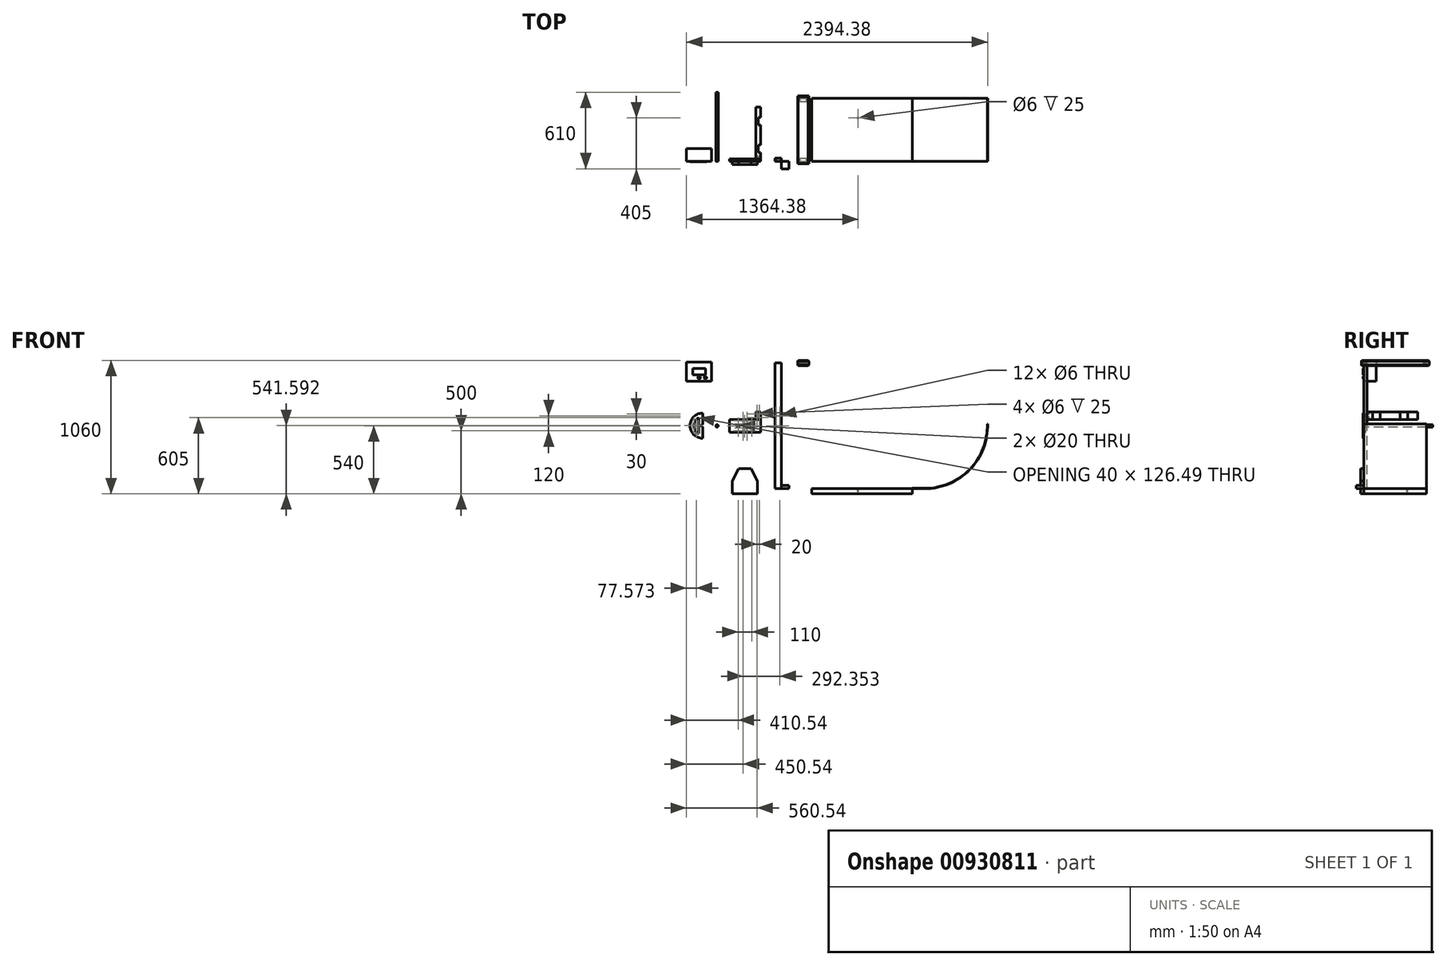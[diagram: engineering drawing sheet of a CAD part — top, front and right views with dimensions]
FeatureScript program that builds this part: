
annotation { "Feature Type Name" : "Feature", "Feature Type Description" : "" }
export const myFeature = defineFeature(function(context is Context, id is Id, definition is map)
    precondition{}
    {
        {
            var Q0;
            Q0=qCreatedBy(makeId("Top.planeOp"),FACE);
            var sketch = newSketch(context, id + "F0", { "sketchPlane" : qUnion([Q0])});
            skLineSegment(sketch, "E0.bottom", {"start": v(-400, 250) * mm, "end": v(400, 250) * mm});
            skLineSegment(sketch, "E0.top", {"start": v(-400, -250) * mm, "end": v(400, -250) * mm});
            skLineSegment(sketch, "E0.left", {"start": v(-400, 250) * mm, "end": v(-400, -250) * mm});
            skLineSegment(sketch, "E0.right", {"start": v(400, 250) * mm, "end": v(400, -250) * mm});
            skPoint(sketch, "E0.middle", {"position": v(0, 0) * mm});
            skSolve(sketch);
        }
        {
            var Q0;
            Q0 = qSketchRegion(id + "F0", true);
            extrude(context, id + "F1", {"entities" : qUnion([Q0]), "depth" : 40 * mm, "offsetDistance" : 25 * mm});
        }
        {
            var Q0;
            Q0=makeQuery(id+"F1.opExtrude","SWEPT_FACE",FACE,{"disambiguationData":[OSD([sQuery(id+"F0.wireOp",EDGE,"E0.top")])]});
            var sketch = newSketch(context, id + "F2", { "sketchPlane" : qUnion([Q0])});
            skLineSegment(sketch, "E1.bottom", {"start": v(-641.49, 40) * mm, "end": v(-691.49, 40) * mm});
            skLineSegment(sketch, "E1.top", {"start": v(-641.49, 1040) * mm, "end": v(-691.49, 1040) * mm});
            skLineSegment(sketch, "E1.left", {"start": v(-641.49, 40) * mm, "end": v(-641.49, 1040) * mm});
            skLineSegment(sketch, "E1.right", {"start": v(-691.49, 40) * mm, "end": v(-691.49, 1040) * mm});
            skCircle(sketch, "E2", {"center": v(-651.49, 620) * mm, "radius": 3 * mm});
            skCircle(sketch, "E3", {"center": v(-681.49, 620) * mm, "radius": 3 * mm});
            skCircle(sketch, "E4.MirrorC", {"center": v(-651.49, 540) * mm, "radius": 3 * mm});
            skCircle(sketch, "E5.MirrorC", {"center": v(-681.49, 540) * mm, "radius": 3 * mm});
            skSolve(sketch);
        }
        {
            var Q0;
            Q0=makeQuery(id+"F2.imprint","IMPRINT",FACE,{"disambiguationData":[TD([[makeQuery(id+"F2.imprint","IMPRINT",EDGE,{"derivedFrom":sQuery(id+"F2.wireOp",EDGE,"E1.bottom")}),-1.0]])]});
            extrude(context, id + "F3", {"entities" : qUnion([Q0]), "oppositeDirection" : true, "depth" : 25 * mm, "offsetDistance" : 25 * mm});
        }
        {
            var Q0;
            Q0=makeQuery(id+"F1.opExtrude","SWEPT_FACE",FACE,{"disambiguationData":[OSD([sQuery(id+"F0.wireOp",EDGE,"E0.top")])]});
            var sketch = newSketch(context, id + "F4", { "sketchPlane" : qUnion([Q0])});
            skLineSegment(sketch, "E6.bottom", {"start": v(-829.9, 0) * mm, "end": v(-1029.9, 0) * mm});
            skLineSegment(sketch, "E6.top", {"start": v(-879.9, 200) * mm, "end": v(-979.9, 200) * mm});
            skLineSegment(sketch, "E6.left", {"start": v(-829.9, 0) * mm, "end": v(-829.9, 100) * mm});
            skLineSegment(sketch, "E6.right", {"start": v(-1029.9, 0) * mm, "end": v(-1029.9, 100) * mm});
            skLineSegment(sketch, "E7", {"start": v(-1029.9, 100) * mm, "end": v(-979.9, 200) * mm});
            skLineSegment(sketch, "E8", {"start": v(-829.9, 100) * mm, "end": v(-879.9, 200) * mm});
            skSolve(sketch);
        }
        {
            var Q0;
            Q0 = qSketchRegion(id + "F4", true);
            extrude(context, id + "F5", {"entities" : qUnion([Q0]), "depth" : 25 * mm, "offsetDistance" : 25 * mm});
        }
        {
            var Q0;
            Q0=makeQuery(id+"F3.opExtrude","CAP_FACE",FACE,{"disambiguationData":[OSD([sQuery(id+"F2.wireOp",EDGE,"E1.bottom"),sQuery(id+"F2.wireOp",EDGE,"E1.top"),sQuery(id+"F2.wireOp",EDGE,"E1.left"),sQuery(id+"F2.wireOp",EDGE,"E1.right")])],"isStart":true});
            var sketch = newSketch(context, id + "F6", { "sketchPlane" : qUnion([Q0])});
            skLineSegment(sketch, "E9.bottom", {"start": v(-1053.84, 590) * mm, "end": v(-803.84, 590) * mm});
            skLineSegment(sketch, "E9.top", {"start": v(-1053.84, 490) * mm, "end": v(-803.84, 490) * mm});
            skLineSegment(sketch, "E9.left", {"start": v(-1053.84, 590) * mm, "end": v(-1053.84, 490) * mm});
            skLineSegment(sketch, "E9.right", {"start": v(-803.84, 590) * mm, "end": v(-803.84, 490) * mm});
            skPoint(sketch, "E9.middle", {"position": v(-928.84, 540) * mm});
            skPoint(sketch, "E9.middle.positionSnap0", {"position": v(-691.49, 540) * mm});
            skPoint(sketch, "E9.centerSnap0", {"position": v(-691.49, 540) * mm});
            skCircle(sketch, "E10", {"center": v(-873.84, 540) * mm, "radius": 10 * mm});
            skCircle(sketch, "E11", {"center": v(-983.84, 540) * mm, "radius": 10 * mm});
            skCircle(sketch, "E12", {"center": v(-943.84, 580) * mm, "radius": 3 * mm});
            skCircle(sketch, "E13", {"center": v(-913.84, 580) * mm, "radius": 3 * mm});
            skCircle(sketch, "E14.MirrorC", {"center": v(-943.84, 500) * mm, "radius": 3 * mm});
            skCircle(sketch, "E15.MirrorC", {"center": v(-913.84, 500) * mm, "radius": 3 * mm});
            skPoint(sketch, "E16.middle", {"position": v(-933.84, 540) * mm});
            skCircle(sketch, "E17", {"center": v(-913.84, 555) * mm, "radius": 3 * mm});
            skCircle(sketch, "E18", {"center": v(-913.84, 525) * mm, "radius": 3 * mm});
            skCircle(sketch, "E19", {"center": v(-933.84, 525) * mm, "radius": 3 * mm});
            skCircle(sketch, "E20", {"center": v(-933.84, 555) * mm, "radius": 3 * mm});
            skSolve(sketch);
        }
        {
            var Q0;
            Q0=makeQuery(id+"F6.imprint","IMPRINT",FACE,{"disambiguationData":[TD([[makeQuery(id+"F6.imprint","IMPRINT",EDGE,{"derivedFrom":sQuery(id+"F6.wireOp",EDGE,"E9.bottom")}),-1.0]])]});
            extrude(context, id + "F7", {"entities" : qUnion([Q0]), "oppositeDirection" : true, "depth" : 20 * mm, "offsetDistance" : 25 * mm});
        }
        {
            var Q0;
            Q0=makeQuery(id+"F7.opExtrude","CAP_FACE",FACE,{"disambiguationData":[OSD([sQuery(id+"F6.wireOp",EDGE,"E9.bottom"),sQuery(id+"F6.wireOp",EDGE,"E9.top"),sQuery(id+"F6.wireOp",EDGE,"E9.left"),sQuery(id+"F6.wireOp",EDGE,"E9.right"),sQuery(id+"F6.wireOp",EDGE,"E10"),sQuery(id+"F6.wireOp",EDGE,"E11"),sQuery(id+"F6.wireOp",EDGE,"E12"),sQuery(id+"F6.wireOp",EDGE,"E13"),sQuery(id+"F6.wireOp",EDGE,"E14.MirrorC"),sQuery(id+"F6.wireOp",EDGE,"E15.MirrorC")])],"isStart":true});
            var sketch = newSketch(context, id + "F8", { "sketchPlane" : qUnion([Q0])});
            skCircle(sketch, "E21", {"center": v(-1152.55, 540) * mm, "radius": 10 * mm});
            skPoint(sketch, "E21.centerSnap0", {"position": v(-1053.84, 540) * mm});
            skSolve(sketch);
        }
        {
            var Q0;
            Q0 = qSketchRegion(id + "F8", true);
            extrude(context, id + "F9", {"entities" : qUnion([Q0]), "oppositeDirection" : true, "depth" : 550 * mm, "offsetDistance" : 25 * mm});
        }
        {
            var Q0;
            Q0=makeQuery(id+"F7.opExtrude","SWEPT_FACE",FACE,{"disambiguationData":[OSD([sQuery(id+"F6.wireOp",EDGE,"E9.bottom")])]});
            var sketch = newSketch(context, id + "F10", { "sketchPlane" : qUnion([Q0])});
            skLineSegment(sketch, "E22.bottom", {"start": v(-803.84, -230) * mm, "end": v(-843.84, -230) * mm});
            skLineSegment(sketch, "E22.top", {"start": v(-803.84, 180) * mm, "end": v(-843.84, 180) * mm});
            skLineSegment(sketch, "E22.left", {"start": v(-803.84, -230) * mm, "end": v(-803.84, -180) * mm});
            skLineSegment(sketch, "E22.right", {"start": v(-843.84, -230) * mm, "end": v(-843.84, 180) * mm});
            skLineSegment(sketch, "E23", {"start": v(-803.84, -180) * mm, "end": v(-823.84, -180) * mm});
            skLineSegment(sketch, "E24", {"start": v(-823.84, -180) * mm, "end": v(-823.84, -120) * mm});
            skLineSegment(sketch, "E25", {"start": v(-823.84, -120) * mm, "end": v(-803.84, -120) * mm});
            skLineSegment(sketch, "E26.trimOffspring", {"start": v(-803.84, -120) * mm, "end": v(-803.84, 40) * mm});
            skLineSegment(sketch, "E27", {"start": v(-803.84, 100) * mm, "end": v(-823.84, 100) * mm});
            skLineSegment(sketch, "E28", {"start": v(-823.84, 100) * mm, "end": v(-823.84, 40) * mm});
            skLineSegment(sketch, "E29", {"start": v(-823.84, 40) * mm, "end": v(-803.84, 40) * mm});
            skLineSegment(sketch, "E30.trimOffspring", {"start": v(-803.84, 100) * mm, "end": v(-803.84, 180) * mm});
            skSolve(sketch);
        }
        {
            var Q0;
            Q0 = qSketchRegion(id + "F10", true);
            extrude(context, id + "F11", {"entities" : qUnion([Q0]), "operationType" : NewBodyOperationType.ADD, "depth" : 60 * mm, "offsetDistance" : 25 * mm});
        }
        {
            var Q0;
            Q0=makeQuery(id+"F11.opExtrude","SWEPT_FACE",FACE,{"disambiguationData":[OSD([sQuery(id+"F10.wireOp",EDGE,"E22.bottom")])]});
            var sketch = newSketch(context, id + "F12", { "sketchPlane" : qUnion([Q0])});
            skCircle(sketch, "E31", {"center": v(-833.84, 635) * mm, "radius": 3 * mm});
            skCircle(sketch, "E32", {"center": v(-813.84, 635) * mm, "radius": 3 * mm});
            skCircle(sketch, "E33", {"center": v(-833.84, 605) * mm, "radius": 3 * mm});
            skCircle(sketch, "E34", {"center": v(-813.84, 605) * mm, "radius": 3 * mm});
            skSolve(sketch);
        }
        {
            var Q0;
            Q0 = qSketchRegion(id + "F12", true);
            extrude(context, id + "F13", {"entities" : qUnion([Q0]), "operationType" : NewBodyOperationType.REMOVE, "oppositeDirection" : true, "depth" : 25 * mm, "offsetDistance" : 25 * mm});
        }
        {
            var Q0;
            Q0=makeQuery(id+"F3.opExtrude","CAP_FACE",FACE,{"disambiguationData":[OSD([sQuery(id+"F2.wireOp",EDGE,"E1.bottom"),sQuery(id+"F2.wireOp",EDGE,"E1.top"),sQuery(id+"F2.wireOp",EDGE,"E1.left"),sQuery(id+"F2.wireOp",EDGE,"E1.right"),sQuery(id+"F2.wireOp",EDGE,"E2"),sQuery(id+"F2.wireOp",EDGE,"E3"),sQuery(id+"F2.wireOp",EDGE,"E4.MirrorC"),sQuery(id+"F2.wireOp",EDGE,"E5.MirrorC")])],"isStart":true});
            var sketch = newSketch(context, id + "F14", { "sketchPlane" : qUnion([Q0])});
            skLineSegment(sketch, "E35.bottom", {"start": v(-641.49, 40) * mm, "end": v(-581.49, 40) * mm});
            skLineSegment(sketch, "E35.top", {"start": v(-641.49, 65) * mm, "end": v(-581.49, 65) * mm});
            skLineSegment(sketch, "E35.left", {"start": v(-641.49, 40) * mm, "end": v(-641.49, 65) * mm});
            skLineSegment(sketch, "E35.right", {"start": v(-581.49, 40) * mm, "end": v(-581.49, 65) * mm});
            skSolve(sketch);
        }
        {
            var Q0;
            Q0 = qSketchRegion(id + "F14", true);
            extrude(context, id + "F15", {"entities" : qUnion([Q0]), "depth" : 60 * mm, "offsetDistance" : 25 * mm});
        }
        {
            var Q0;
            Q0=makeQuery(id+"F1.opExtrude","CAP_FACE",FACE,{"disambiguationData":[OSD([sQuery(id+"F0.wireOp",EDGE,"E0.bottom"),sQuery(id+"F0.wireOp",EDGE,"E0.top"),sQuery(id+"F0.wireOp",EDGE,"E0.left"),sQuery(id+"F0.wireOp",EDGE,"E0.right")])],"isStart":false});
            var sketch = newSketch(context, id + "F16", { "sketchPlane" : qUnion([Q0])});
            skCircle(sketch, "E36", {"center": v(-30, 95) * mm, "radius": 3 * mm});
            skSolve(sketch);
        }
        {
            var Q0;
            Q0 = qSketchRegion(id + "F16", true);
            extrude(context, id + "F17", {"entities" : qUnion([Q0]), "operationType" : NewBodyOperationType.REMOVE, "oppositeDirection" : true, "depth" : 25 * mm, "offsetDistance" : 25 * mm});
        }
        {
            var Q0;
            Q0=makeQuery(id+"F3.opExtrude","SWEPT_FACE",FACE,{"disambiguationData":[OSD([sQuery(id+"F2.wireOp",EDGE,"E1.top")])]});
            var sketch = newSketch(context, id + "F18", { "sketchPlane" : qUnion([Q0])});
            skLineSegment(sketch, "E37.bottom", {"start": v(-491.35, -250) * mm, "end": v(-441.35, -250) * mm});
            skLineSegment(sketch, "E37.top", {"start": v(-491.35, 250) * mm, "end": v(-441.35, 250) * mm});
            skLineSegment(sketch, "E37.left", {"start": v(-491.35, -250) * mm, "end": v(-491.35, -225) * mm});
            skLineSegment(sketch, "E37.right", {"start": v(-441.35, -250) * mm, "end": v(-441.35, -225) * mm});
            skLineSegment(sketch, "E38.0", {"start": v(-511.35, 270) * mm, "end": v(-421.35, 270) * mm});
            skLineSegment(sketch, "E38.1", {"start": v(-511.35, -270) * mm, "end": v(-511.35, 270) * mm});
            skLineSegment(sketch, "E38.2", {"start": v(-511.35, -270) * mm, "end": v(-421.35, -270) * mm});
            skLineSegment(sketch, "E38.3", {"start": v(-421.35, -270) * mm, "end": v(-421.35, 270) * mm});
            skLineSegment(sketch, "E39", {"start": v(-491.35, -225) * mm, "end": v(-441.35, -225) * mm});
            skLineSegment(sketch, "E40", {"start": v(-491.35, 225) * mm, "end": v(-441.35, 225) * mm});
            skLineSegment(sketch, "E41.trimOffspring", {"start": v(-491.35, 225) * mm, "end": v(-491.35, 250) * mm});
            skLineSegment(sketch, "E42.trimOffspring", {"start": v(-441.35, 225) * mm, "end": v(-441.35, 250) * mm});
            skSolve(sketch);
        }
        {
            var Q0;
            Q0 = qSketchRegion(id + "F18", true);
            extrude(context, id + "F19", {"entities" : qUnion([Q0]), "oppositeDirection" : true, "depth" : 20 * mm, "offsetDistance" : 25 * mm});
        }
        {
            var Q0;
            Q0 = qSketchRegion(id + "F18", true);
            var Q1;
            Q1=makeQuery(id+"F18.imprint","IMPRINT",FACE,{"disambiguationData":[TD([[makeQuery(id+"F18.imprint","IMPRINT",EDGE,{"derivedFrom":sQuery(id+"F18.wireOp",EDGE,"E37.top")}),-1.0]])]});
            var Q2;
            Q2=makeQuery(id+"F18.imprint","IMPRINT",FACE,{"disambiguationData":[TD([[makeQuery(id+"F18.imprint","IMPRINT",EDGE,{"derivedFrom":sQuery(id+"F18.wireOp",EDGE,"E37.bottom")}),1.0]])]});
            extrude(context, id + "F20", {"entities" : qUnion([Q0, Q1, Q2]), "operationType" : NewBodyOperationType.ADD, "depth" : 20 * mm, "offsetDistance" : 25 * mm});
        }
        {
            var Q0;
            Q0=makeQuery(id+"F20.opExtrude","CAP_EDGE",EDGE,{"disambiguationData":[OSD([sQuery(id+"F18.wireOp",EDGE,"E38.1")])],"isStart":false});
            var Q1;
            Q1=makeQuery(id+"F20.opExtrude","CAP_EDGE",EDGE,{"disambiguationData":[OSD([sQuery(id+"F18.wireOp",EDGE,"E38.0")])],"isStart":false});
            var Q2;
            Q2=makeQuery(id+"F20.opExtrude","CAP_EDGE",EDGE,{"disambiguationData":[OSD([sQuery(id+"F18.wireOp",EDGE,"E38.3")])],"isStart":false});
            var Q3;
            Q3=makeQuery(id+"F20.opExtrude","CAP_EDGE",EDGE,{"disambiguationData":[OSD([sQuery(id+"F18.wireOp",EDGE,"E38.2")])],"isStart":false});
            var Q4;
            Q4=makeQuery(id+"F19.opExtrude","CAP_EDGE",EDGE,{"disambiguationData":[OSD([sQuery(id+"F18.wireOp",EDGE,"E38.2")])],"isStart":false});
            var Q5;
            Q5=makeQuery(id+"F19.opExtrude","CAP_EDGE",EDGE,{"disambiguationData":[OSD([sQuery(id+"F18.wireOp",EDGE,"E38.1")])],"isStart":false});
            var Q6;
            Q6=makeQuery(id+"F19.opExtrude","CAP_EDGE",EDGE,{"disambiguationData":[OSD([sQuery(id+"F18.wireOp",EDGE,"E38.3")])],"isStart":false});
            var Q7;
            Q7=makeQuery(id+"F19.opExtrude","CAP_EDGE",EDGE,{"disambiguationData":[OSD([sQuery(id+"F18.wireOp",EDGE,"E38.0")])],"isStart":false});
            chamfer(context, id + "F21", {"entities" : qUnion([Q0, Q1, Q2, Q3, Q4, Q5, Q6, Q7]), "width" : 5 * mm, "tangentPropagation" : true});
        }
        {
            var Q0;
            Q0=makeQuery(id+"F9.opExtrude","CAP_FACE",FACE,{"disambiguationData":[OSD([sQuery(id+"F8.wireOp",EDGE,"E21")])],"isStart":true});
            var sketch = newSketch(context, id + "F22", { "sketchPlane" : qUnion([Q0])});
            skArc(sketch, "E43", {"start": v(-1266.8, 641.6) * mm, "mid": v(-1366.8, 541.6) * mm, "end": v(-1266.8, 441.6) * mm});
            skArc(sketch, "E44", {"start": v(-1296.8, 604.84) * mm, "mid": v(-1336.8, 541.6) * mm, "end": v(-1296.8, 478.35) * mm});
            skLineSegment(sketch, "E45", {"start": v(-1266.8, 641.6) * mm, "end": v(-1266.8, 551.6) * mm});
            skLineSegment(sketch, "E46", {"start": v(-1296.8, 604.84) * mm, "end": v(-1296.8, 478.35) * mm});
            skArc(sketch, "E47", {"start": v(-1266.8, 551.6) * mm, "mid": v(-1276.8, 541.6) * mm, "end": v(-1266.8, 531.6) * mm});
            skLineSegment(sketch, "E48.trimOffspring", {"start": v(-1266.8, 531.6) * mm, "end": v(-1266.8, 441.6) * mm});
            skSolve(sketch);
        }
        {
            var Q0;
            Q0 = qSketchRegion(id + "F22", true);
            extrude(context, id + "F23", {"entities" : qUnion([Q0]), "depth" : 5 * mm, "offsetDistance" : 25 * mm});
        }
        {
            var Q0;
            {var subQ2=sQuery(id+"F14.wireOp",EDGE,"E35.left");Q0=makeQuery(id+"F14.imprint","IMPRINT",FACE,{"disambiguationData":[TD([[makeQuery(id+"F14.imprint","IMPRINT",EDGE,{"derivedFrom":subQ2}),1.0]])]});}
            var sketch = newSketch(context, id + "F24", { "sketchPlane" : qUnion([Q0])});
            skLineSegment(sketch, "E49.bottom", {"start": v(-1194.38, 1046.37) * mm, "end": v(-1394.38, 1046.37) * mm});
            skLineSegment(sketch, "E49.top", {"start": v(-1194.38, 896.37) * mm, "end": v(-1394.38, 896.37) * mm});
            skLineSegment(sketch, "E49.left", {"start": v(-1194.38, 1046.37) * mm, "end": v(-1194.38, 896.37) * mm});
            skLineSegment(sketch, "E49.right", {"start": v(-1394.38, 1046.37) * mm, "end": v(-1394.38, 896.37) * mm});
            skPoint(sketch, "E49.middle", {"position": v(-1294.38, 971.37) * mm});
            skLineSegment(sketch, "E50.bottom", {"start": v(-1344.38, 996.37) * mm, "end": v(-1244.38, 996.37) * mm});
            skLineSegment(sketch, "E50.top", {"start": v(-1344.38, 946.37) * mm, "end": v(-1244.38, 946.37) * mm});
            skLineSegment(sketch, "E50.left", {"start": v(-1344.38, 996.37) * mm, "end": v(-1344.38, 946.37) * mm});
            skLineSegment(sketch, "E50.right", {"start": v(-1244.38, 996.37) * mm, "end": v(-1244.38, 946.37) * mm});
            skCircle(sketch, "E51", {"center": v(-1244.38, 923.12) * mm, "radius": 10 * mm});
            skCircle(sketch, "E52", {"center": v(-1294.38, 923.12) * mm, "radius": 10 * mm});
            skPoint(sketch, "E52.centerSnap0", {"position": v(-1294.38, 946.37) * mm});
            skSolve(sketch);
        }
        {
            var Q0;
            Q0 = qSketchRegion(id + "F24", true);
            var Q1;
            Q1=makeQuery(id+"F24.imprint","IMPRINT",FACE,{"disambiguationData":[TD([[makeQuery(id+"F24.imprint","IMPRINT",EDGE,{"derivedFrom":sQuery(id+"F24.wireOp",EDGE,"E49.bottom")}),1.0]])]});
            var Q2;
            Q2=makeQuery(id+"F24.imprint","IMPRINT",FACE,{"disambiguationData":[TD([[makeQuery(id+"F24.imprint","IMPRINT",EDGE,{"derivedFrom":sQuery(id+"F24.wireOp",EDGE,"E50.bottom")}),-1.0]])]});
            var Q3;
            Q3=makeQuery(id+"F24.imprint","IMPRINT",FACE,{"disambiguationData":[TD([[makeQuery(id+"F24.imprint","IMPRINT",EDGE,{"derivedFrom":sQuery(id+"F24.wireOp",EDGE,"E51")}),1.0]])]});
            var Q4;
            Q4=makeQuery(id+"F24.imprint","IMPRINT",FACE,{"disambiguationData":[TD([[makeQuery(id+"F24.imprint","IMPRINT",EDGE,{"derivedFrom":sQuery(id+"F24.wireOp",EDGE,"E52")}),1.0]])]});
            extrude(context, id + "F25", {"entities" : qUnion([Q0, Q1, Q2, Q3, Q4]), "oppositeDirection" : true, "depth" : 100 * mm, "offsetDistance" : 25 * mm});
        }
        {
            var Q0;
            Q0=makeQuery(id+"F24.imprint","IMPRINT",FACE,{"disambiguationData":[TD([[makeQuery(id+"F24.imprint","IMPRINT",EDGE,{"derivedFrom":sQuery(id+"F24.wireOp",EDGE,"E50.bottom")}),-1.0]])]});
            var Q1;
            Q1=makeQuery(id+"F24.imprint","IMPRINT",FACE,{"disambiguationData":[TD([[makeQuery(id+"F24.imprint","IMPRINT",EDGE,{"derivedFrom":sQuery(id+"F24.wireOp",EDGE,"E52")}),1.0]])]});
            var Q2;
            Q2=makeQuery(id+"F24.imprint","IMPRINT",FACE,{"disambiguationData":[TD([[makeQuery(id+"F24.imprint","IMPRINT",EDGE,{"derivedFrom":sQuery(id+"F24.wireOp",EDGE,"E51")}),1.0]])]});
            extrude(context, id + "F26", {"entities" : qUnion([Q0, Q1, Q2]), "operationType" : NewBodyOperationType.ADD, "depth" : 5 * mm, "offsetDistance" : 25 * mm});
        }
        {
            var Q0;
            Q0=makeQuery(id+"F1.opExtrude","SWEPT_FACE",FACE,{"disambiguationData":[OSD([sQuery(id+"F0.wireOp",EDGE,"E0.top")])]});
            var sketch = newSketch(context, id + "F27", { "sketchPlane" : qUnion([Q0])});
            skLineSegment(sketch, "E53", {"start": v(400, 40) * mm, "end": v(500, 40) * mm});
            skArc(sketch, "E54", {"start": v(500, 40) * mm, "mid": v(859.17, 192.15) * mm, "end": v(999.74, 556.01) * mm});
            skArc(sketch, "E55.0", {"start": v(500, 43) * mm, "mid": v(857.02, 194.24) * mm, "end": v(996.75, 555.92) * mm});
            skLineSegment(sketch, "E55.1", {"start": v(400, 43) * mm, "end": v(500, 43) * mm});
            skLineSegment(sketch, "E56", {"start": v(999.74, 556.01) * mm, "end": v(996.75, 555.92) * mm});
            skLineSegment(sketch, "E57", {"start": v(400, 43) * mm, "end": v(400, 40) * mm});
            skSolve(sketch);
        }
        {
            var Q0;
            Q0 = qSketchRegion(id + "F27", true);
            extrude(context, id + "F28", {"entities" : qUnion([Q0]), "oppositeDirection" : true, "depth" : 500 * mm, "offsetDistance" : 25 * mm});
        }
    });
